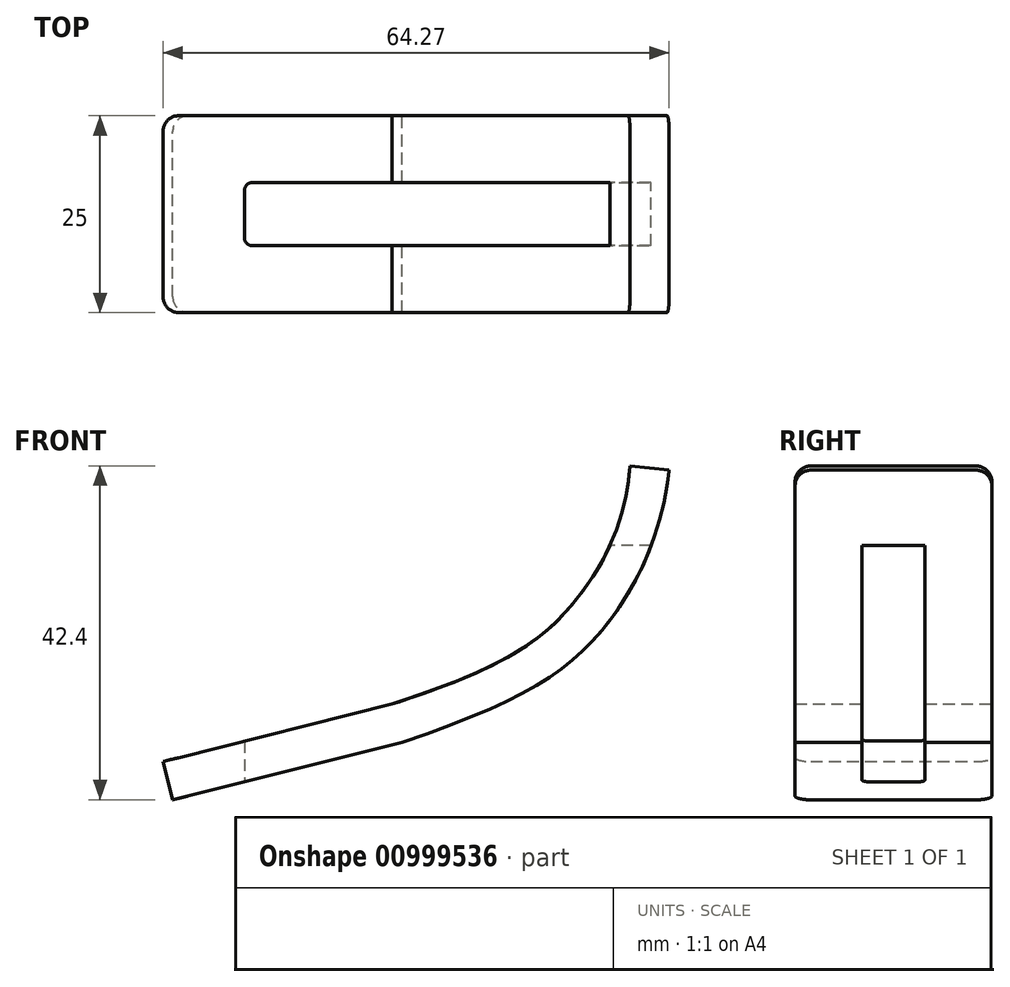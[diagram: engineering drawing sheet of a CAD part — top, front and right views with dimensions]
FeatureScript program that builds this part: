
annotation { "Feature Type Name" : "Feature", "Feature Type Description" : "" }
export const myFeature = defineFeature(function(context is Context, id is Id, definition is map)
    precondition{}
    {
        {
            var Q0;
            Q0=qCreatedBy(makeId("Front.planeOp"),FACE);
            var sketch = newSketch(context, id + "F0", { "sketchPlane" : qUnion([Q0])});
            skFitSpline(sketch, "E0", {"points": [v(0, 0) * mm, v(24.94, 13.72) * mm, v(33.95, 34.6) * mm], "startDerivative": vector(79.5, 27.36) * mm, "endDerivative": vector(5.82, 55.18) * mm});
            skFitSpline(sketch, "E1.0", {"points": [v(-1.63, 4.73) * mm, v(1.63, 5.85) * mm, v(7.2, 7.9) * mm, v(12.2, 10.17) * mm, v(15.29, 11.94) * mm, v(17.24, 13.28) * mm, v(18.94, 14.68) * mm, v(20.24, 15.95) * mm, v(21.25, 17.08) * mm, v(22.25, 18.28) * mm, v(23.93, 20.54) * mm, v(26.07, 24.22) * mm, v(28, 29.3) * mm, v(28.76, 33.1) * mm, v(28.98, 35.12) * mm]});
            skLineSegment(sketch, "E2", {"start": v(33.95, 34.6) * mm, "end": v(28.98, 35.12) * mm});
            skLineSegment(sketch, "E3", {"start": v(-1.22, 4.87) * mm, "end": v(0, 0) * mm});
            skLineSegment(sketch, "E4", {"start": v(-1.22, 4.87) * mm, "end": v(-30.32, -2.41) * mm});
            skLineSegment(sketch, "E5", {"start": v(-30.32, -2.41) * mm, "end": v(-29.1, -7.28) * mm});
            skLineSegment(sketch, "E6", {"start": v(-29.1, -7.28) * mm, "end": v(0, 0) * mm});
            skSolve(sketch);
        }
        {
            var Q0;
            Q0=makeQuery(id+"F0.imprint","IMPRINT",FACE,{"disambiguationData":[TD([[makeQuery(id+"F0.imprint","IMPRINT",EDGE,{"derivedFrom":sQuery(id+"F0.wireOp",EDGE,"E0")}),1.0]])]});
            var Q1;
            Q1=makeQuery(id+"F0.imprint","IMPRINT",FACE,{"disambiguationData":[TD([[makeQuery(id+"F0.imprint","IMPRINT",EDGE,{"derivedFrom":sQuery(id+"F0.wireOp",EDGE,"E3")}),-1.0]])]});
            extrude(context, id + "F1", {"entities" : qUnion([Q0, Q1]), "depth" : 12.5 * mm, "offsetDistance" : 25 * mm, "hasSecondDirection" : true, "secondDirectionOppositeDirection" : true, "secondDirectionDepth" : 12.5 * mm});
        }
        {
            var Q0;
            Q0=makeQuery(id+"F1.opExtrude","CAP_EDGE",EDGE,{"disambiguationData":[OSD([sQuery(id+"F0.wireOp",EDGE,"E2")])],"isStart":false});
            var Q1;
            Q1=makeQuery(id+"F1.opExtrude","CAP_EDGE",EDGE,{"disambiguationData":[OSD([sQuery(id+"F0.wireOp",EDGE,"E2")])],"isStart":true});
            var Q2;
            Q2=makeQuery(id+"F1.opExtrude","CAP_EDGE",EDGE,{"disambiguationData":[OSD([sQuery(id+"F0.wireOp",EDGE,"E5")])],"isStart":false});
            var Q3;
            Q3=makeQuery(id+"F1.opExtrude","CAP_EDGE",EDGE,{"disambiguationData":[OSD([sQuery(id+"F0.wireOp",EDGE,"E5")])],"isStart":true});
            fillet(context, id + "F2", {"entities" : qUnion([Q0, Q1, Q2, Q3]), "radius" : 2 * mm, "tangentPropagation" : true, "allowEdgeOverflow" : false});
        }
        {
            var Q0;
            Q0=qCreatedBy(makeId("Top.planeOp"),FACE);
            var sketch = newSketch(context, id + "F3", { "sketchPlane" : qUnion([Q0])});
            skLineSegment(sketch, "E7", {"start": v(0, 0) * mm, "end": v(15, 0) * mm, "construction": true});
            skLineSegment(sketch, "E8.bottom", {"start": v(50, -4) * mm, "end": v(-19, -4) * mm});
            skLineSegment(sketch, "E8.top", {"start": v(50, 4) * mm, "end": v(-19, 4) * mm});
            skLineSegment(sketch, "E8.left", {"start": v(50, -4) * mm, "end": v(50, 4) * mm});
            skLineSegment(sketch, "E8.right", {"start": v(-20, -3) * mm, "end": v(-20, 3) * mm});
            skPoint(sketch, "E8.middle", {"position": v(15, 0) * mm});
            skPoint(sketch, "E9.visualSharp", {"position": v(-20, -4) * mm});
            skArc(sketch, "E9.filletArc", {"start": v(-20, -3) * mm, "mid": v(-19.7, -3.7) * mm, "end": v(-19, -4) * mm});
            skPoint(sketch, "E10.visualSharp", {"position": v(-20, 4) * mm});
            skArc(sketch, "E10.filletArc", {"start": v(-19, 4) * mm, "mid": v(-19.7, 3.7) * mm, "end": v(-20, 3) * mm});
            skSolve(sketch);
        }
        {
            var Q0;
            Q0=makeQuery(id+"F3.imprint","IMPRINT",FACE,{"disambiguationData":[TD([[makeQuery(id+"F3.imprint","IMPRINT",EDGE,{"derivedFrom":sQuery(id+"F3.wireOp",EDGE,"E8.bottom")}),-1.0]])]});
            extrude(context, id + "F4", {"entities" : qUnion([Q0]), "operationType" : NewBodyOperationType.REMOVE, "depth" : 25 * mm, "offsetDistance" : 25 * mm, "hasSecondDirection" : true, "secondDirectionOppositeDirection" : true, "secondDirectionDepth" : 25 * mm});
        }
    });
